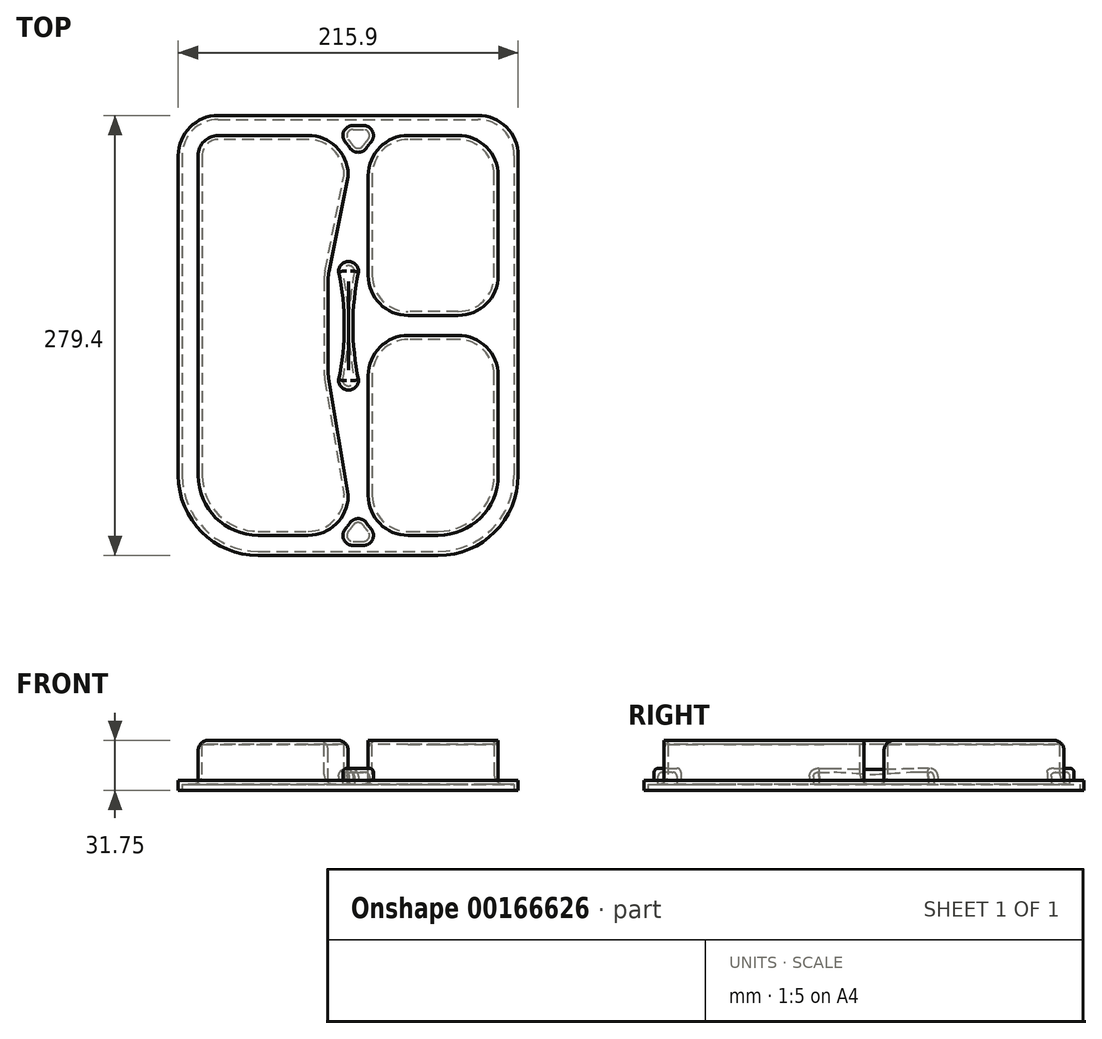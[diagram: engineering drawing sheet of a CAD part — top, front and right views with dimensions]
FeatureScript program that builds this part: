
annotation { "Feature Type Name" : "Feature", "Feature Type Description" : "" }
export const myFeature = defineFeature(function(context is Context, id is Id, definition is map)
    precondition{}
    {
        {
            var Q0;
            Q0=qCreatedBy(makeId("Top.planeOp"),FACE);
            var sketch = newSketch(context, id + "F0", { "sketchPlane" : qUnion([Q0])});
            skLineSegment(sketch, "E0.bottom", {"start": v(-121.24, 224.08) * mm, "end": v(43.86, 224.08) * mm});
            skLineSegment(sketch, "E0.top", {"start": v(-95.84, -55.32) * mm, "end": v(18.46, -55.32) * mm});
            skLineSegment(sketch, "E0.left", {"start": v(-146.64, 198.68) * mm, "end": v(-146.64, -4.52) * mm});
            skLineSegment(sketch, "E0.right", {"start": v(69.26, 198.68) * mm, "end": v(69.26, -4.52) * mm});
            skPoint(sketch, "E1.visualSharp", {"position": v(69.26, 224.08) * mm});
            skArc(sketch, "E1.filletArc", {"start": v(69.26, 198.68) * mm, "mid": v(61.83, 216.64) * mm, "end": v(43.86, 224.08) * mm});
            skPoint(sketch, "E2.visualSharp", {"position": v(-146.64, 224.08) * mm});
            skArc(sketch, "E2.filletArc", {"start": v(-121.24, 224.08) * mm, "mid": v(-139.2, 216.64) * mm, "end": v(-146.64, 198.68) * mm});
            skPoint(sketch, "E3.visualSharp", {"position": v(-146.64, -55.32) * mm});
            skArc(sketch, "E3.filletArc", {"start": v(-146.64, -4.52) * mm, "mid": v(-131.76, -40.44) * mm, "end": v(-95.84, -55.32) * mm});
            skPoint(sketch, "E4.visualSharp", {"position": v(69.26, -55.32) * mm});
            skArc(sketch, "E4.filletArc", {"start": v(18.46, -55.32) * mm, "mid": v(54.39, -40.44) * mm, "end": v(69.26, -4.52) * mm});
            skSolve(sketch);
        }
        {
            var Q0;
            Q0=makeQuery(id+"F0.imprint","IMPRINT",FACE,{"disambiguationData":[TD([[makeQuery(id+"F0.imprint","IMPRINT",EDGE,{"derivedFrom":sQuery(id+"F0.wireOp",EDGE,"E0.bottom")}),-1.0]])]});
            extrude(context, id + "F1", {"entities" : qUnion([Q0]), "depth" : 31.75 * mm});
        }
        {
            var Q0;
            Q0=makeQuery(id+"F1.opExtrude","CAP_FACE",FACE,{"disambiguationData":[OSD([sQuery(id+"F0.wireOp",EDGE,"E0.bottom"),sQuery(id+"F0.wireOp",EDGE,"E0.top"),sQuery(id+"F0.wireOp",EDGE,"E0.left"),sQuery(id+"F0.wireOp",EDGE,"E0.right"),sQuery(id+"F0.wireOp",EDGE,"E1.filletArc"),sQuery(id+"F0.wireOp",EDGE,"E2.filletArc"),sQuery(id+"F0.wireOp",EDGE,"E3.filletArc"),sQuery(id+"F0.wireOp",EDGE,"E4.filletArc")])],"isStart":false});
            var sketch = newSketch(context, id + "F2", { "sketchPlane" : qUnion([Q0])});
            skLineSegment(sketch, "E5.0.0", {"start": v(43.86, 224.08) * mm, "end": v(-121.24, 224.08) * mm});
            skArc(sketch, "E5.0.1", {"start": v(-121.24, 224.08) * mm, "mid": v(-139.2, 216.64) * mm, "end": v(-146.64, 198.68) * mm});
            skLineSegment(sketch, "E5.0.2", {"start": v(-146.64, 198.68) * mm, "end": v(-146.64, -4.52) * mm});
            skArc(sketch, "E5.0.3", {"start": v(-146.64, -4.52) * mm, "mid": v(-131.76, -40.44) * mm, "end": v(-95.84, -55.32) * mm});
            skLineSegment(sketch, "E5.0.4", {"start": v(-95.84, -55.32) * mm, "end": v(18.46, -55.32) * mm});
            skArc(sketch, "E5.0.5", {"start": v(18.46, -55.32) * mm, "mid": v(54.39, -40.44) * mm, "end": v(69.26, -4.52) * mm});
            skLineSegment(sketch, "E5.0.6", {"start": v(69.26, -4.52) * mm, "end": v(69.26, 198.68) * mm});
            skArc(sketch, "E5.0.7", {"start": v(69.26, 198.68) * mm, "mid": v(61.83, 216.64) * mm, "end": v(43.86, 224.08) * mm});
            skArc(sketch, "E6.0", {"start": v(18.46, -42.62) * mm, "mid": v(45.4, -31.46) * mm, "end": v(56.56, -4.52) * mm});
            skLineSegment(sketch, "E6.1", {"start": v(-95.84, -42.62) * mm, "end": v(-64.09, -42.62) * mm});
            skLineSegment(sketch, "E6.2", {"start": v(56.56, -4.52) * mm, "end": v(56.56, 58.98) * mm});
            skArc(sketch, "E6.3", {"start": v(-133.94, -4.52) * mm, "mid": v(-122.78, -31.46) * mm, "end": v(-95.84, -42.62) * mm});
            skLineSegment(sketch, "E6.5", {"start": v(31.16, 211.38) * mm, "end": v(-0.59, 211.38) * mm});
            skArc(sketch, "E6.6", {"start": v(-121.24, 211.38) * mm, "mid": v(-130.22, 207.66) * mm, "end": v(-133.94, 198.68) * mm});
            skLineSegment(sketch, "E6.7", {"start": v(-133.94, 198.68) * mm, "end": v(-133.94, -4.52) * mm});
            skLineSegment(sketch, "E7.0", {"start": v(-25.99, 185.98) * mm, "end": v(-25.99, 122.48) * mm});
            skLineSegment(sketch, "E8", {"start": v(31.16, 97.08) * mm, "end": v(-0.59, 97.08) * mm});
            skLineSegment(sketch, "E9.0", {"start": v(31.16, 84.38) * mm, "end": v(-0.59, 84.38) * mm});
            skPoint(sketch, "E10.orphan", {"position": v(-133.94, 97.08) * mm});
            skLineSegment(sketch, "E11.trimOffspring", {"start": v(-0.59, -42.62) * mm, "end": v(18.46, -42.62) * mm});
            skLineSegment(sketch, "E12.trimOffspring", {"start": v(-64.09, 211.38) * mm, "end": v(-121.24, 211.38) * mm});
            skLineSegment(sketch, "E13.trimOffspring", {"start": v(-25.99, 58.98) * mm, "end": v(-25.99, -17.22) * mm});
            skLineSegment(sketch, "E14.trimOffspring", {"start": v(56.56, 122.48) * mm, "end": v(56.56, 185.98) * mm});
            skPoint(sketch, "E15.visualSharp", {"position": v(-25.99, 211.38) * mm});
            skArc(sketch, "E15.filletArc", {"start": v(-0.59, 211.38) * mm, "mid": v(-18.55, 203.94) * mm, "end": v(-25.99, 185.98) * mm});
            skPoint(sketch, "E16.visualSharp", {"position": v(56.56, 97.08) * mm});
            skArc(sketch, "E16.filletArc", {"start": v(31.16, 97.08) * mm, "mid": v(49.13, 104.52) * mm, "end": v(56.56, 122.48) * mm});
            skPoint(sketch, "E17.visualSharp", {"position": v(-25.99, 97.08) * mm});
            skArc(sketch, "E17.filletArc", {"start": v(-25.99, 122.48) * mm, "mid": v(-18.55, 104.52) * mm, "end": v(-0.59, 97.08) * mm});
            skPoint(sketch, "E18.newPointA", {"position": v(56.56, 198.68) * mm});
            skPoint(sketch, "E18.newPointB", {"position": v(43.86, 211.38) * mm});
            skArc(sketch, "E18.filletArc", {"start": v(56.56, 185.98) * mm, "mid": v(49.13, 203.94) * mm, "end": v(31.16, 211.38) * mm});
            skPoint(sketch, "E19.visualSharp", {"position": v(56.56, 84.38) * mm});
            skArc(sketch, "E19.filletArc", {"start": v(56.56, 58.98) * mm, "mid": v(49.13, 76.94) * mm, "end": v(31.16, 84.38) * mm});
            skPoint(sketch, "E20.visualSharp", {"position": v(-25.99, 84.38) * mm});
            skArc(sketch, "E20.filletArc", {"start": v(-0.59, 84.38) * mm, "mid": v(-18.55, 76.94) * mm, "end": v(-25.99, 58.98) * mm});
            skPoint(sketch, "E21.visualSharp", {"position": v(-25.99, -42.62) * mm});
            skArc(sketch, "E21.filletArc", {"start": v(-25.99, -17.22) * mm, "mid": v(-18.55, -35.18) * mm, "end": v(-0.59, -42.62) * mm});
            skPoint(sketch, "E22.visualSharp", {"position": v(-38.69, -42.62) * mm});
            skArc(sketch, "E22.filletArc", {"start": v(-64.09, -42.62) * mm, "mid": v(-46.36, -35.41) * mm, "end": v(-38.7, -17.87) * mm});
            skPoint(sketch, "E23.visualSharp", {"position": v(-38.69, 211.38) * mm});
            skArc(sketch, "E23.filletArc", {"start": v(-38.7, 186.76) * mm, "mid": v(-46.4, 204.21) * mm, "end": v(-64.09, 211.38) * mm});
            skLineSegment(sketch, "E24", {"start": v(-25.99, 122.48) * mm, "end": v(-25.99, 58.98) * mm});
            skLineSegment(sketch, "E25.MirrorCS", {"start": v(-51.39, 119.96) * mm, "end": v(-51.39, 61.08) * mm});
            skLineSegment(sketch, "E26", {"start": v(-51.04, 56.9) * mm, "end": v(-38.78, -16.67) * mm});
            skLineSegment(sketch, "E27", {"start": v(-50.9, 124.94) * mm, "end": v(-38.82, 185.32) * mm});
            skPoint(sketch, "E28.visualSharp", {"position": v(-51.39, 122.48) * mm});
            skArc(sketch, "E28.filletArc", {"start": v(-50.9, 124.94) * mm, "mid": v(-51.26, 122.46) * mm, "end": v(-51.39, 119.96) * mm});
            skPoint(sketch, "E29.visualSharp", {"position": v(-51.39, 58.98) * mm});
            skArc(sketch, "E29.filletArc", {"start": v(-51.39, 61.08) * mm, "mid": v(-51.3, 58.98) * mm, "end": v(-51.04, 56.9) * mm});
            skPoint(sketch, "E30.visualSharp", {"position": v(-38.69, -17.22) * mm});
            skArc(sketch, "E30.filletArc", {"start": v(-38.7, -17.87) * mm, "mid": v(-38.7, -17.27) * mm, "end": v(-38.78, -16.67) * mm});
            skPoint(sketch, "E31.visualSharp", {"position": v(-38.69, 185.98) * mm});
            skArc(sketch, "E31.filletArc", {"start": v(-38.82, 185.32) * mm, "mid": v(-38.72, 186.03) * mm, "end": v(-38.7, 186.76) * mm});
            skSolve(sketch);
        }
        {
            var Q0;
            Q0=makeQuery(id+"F2.imprint","IMPRINT",FACE,{"disambiguationData":[TD([[makeQuery(id+"F2.imprint","IMPRINT",EDGE,{"derivedFrom":sQuery(id+"F2.wireOp",EDGE,"E5.0.0")}),-1.0]])]});
            extrude(context, id + "F3", {"entities" : qUnion([Q0]), "operationType" : NewBodyOperationType.REMOVE, "oppositeDirection" : true, "depth" : 25.4 * mm});
        }
        {
            var Q0;
            Q0=makeQuery(id+"F3.boolean.opBoolean","COPY",FACE,{"derivedFrom":makeQuery(id+"F3.opExtrude","CAP_FACE",FACE,{"disambiguationData":[OSD([sQuery(id+"F2.wireOp",EDGE,"E5.0.0"),sQuery(id+"F2.wireOp",EDGE,"E5.0.1"),sQuery(id+"F2.wireOp",EDGE,"E5.0.2"),sQuery(id+"F2.wireOp",EDGE,"E5.0.3"),sQuery(id+"F2.wireOp",EDGE,"E5.0.4"),sQuery(id+"F2.wireOp",EDGE,"E5.0.5"),sQuery(id+"F2.wireOp",EDGE,"E5.0.6"),sQuery(id+"F2.wireOp",EDGE,"E5.0.7"),sQuery(id+"F2.wireOp",EDGE,"E6.0"),sQuery(id+"F2.wireOp",EDGE,"E6.1"),sQuery(id+"F2.wireOp",EDGE,"E6.2"),sQuery(id+"F2.wireOp",EDGE,"E6.3"),sQuery(id+"F2.wireOp",EDGE,"E6.5"),sQuery(id+"F2.wireOp",EDGE,"E6.6"),sQuery(id+"F2.wireOp",EDGE,"E6.7"),sQuery(id+"F2.wireOp",EDGE,"E7.0"),sQuery(id+"F2.wireOp",EDGE,"E8"),sQuery(id+"F2.wireOp",EDGE,"E9.0"),sQuery(id+"F2.wireOp",EDGE,"E11.trimOffspring"),sQuery(id+"F2.wireOp",EDGE,"E12.trimOffspring"),sQuery(id+"F2.wireOp",EDGE,"E13.trimOffspring"),sQuery(id+"F2.wireOp",EDGE,"E14.trimOffspring"),sQuery(id+"F2.wireOp",EDGE,"E15.filletArc"),sQuery(id+"F2.wireOp",EDGE,"E16.filletArc"),sQuery(id+"F2.wireOp",EDGE,"E17.filletArc"),sQuery(id+"F2.wireOp",EDGE,"E18.filletArc"),sQuery(id+"F2.wireOp",EDGE,"E19.filletArc"),sQuery(id+"F2.wireOp",EDGE,"E20.filletArc"),sQuery(id+"F2.wireOp",EDGE,"E21.filletArc"),sQuery(id+"F2.wireOp",EDGE,"E22.filletArc"),sQuery(id+"F2.wireOp",EDGE,"E23.filletArc"),sQuery(id+"F2.wireOp",EDGE,"E25.MirrorCS"),sQuery(id+"F2.wireOp",EDGE,"E26"),sQuery(id+"F2.wireOp",EDGE,"E27"),sQuery(id+"F2.wireOp",EDGE,"E28.filletArc"),sQuery(id+"F2.wireOp",EDGE,"E29.filletArc"),sQuery(id+"F2.wireOp",EDGE,"E30.filletArc"),sQuery(id+"F2.wireOp",EDGE,"E31.filletArc")])],"isStart":false})});
            var sketch = newSketch(context, id + "F4", { "sketchPlane" : qUnion([Q0])});
            skPoint(sketch, "E32.orphan", {"position": v(-15.61, 124.94) * mm});
            skPoint(sketch, "E33.orphan", {"position": v(-25.99, 185.98) * mm});
            skArc(sketch, "E34", {"start": v(-32.08, 124.94) * mm, "mid": v(-38.44, 131.3) * mm, "end": v(-44.8, 124.94) * mm});
            skArc(sketch, "E35.MirrorC", {"start": v(-32.08, 56.1) * mm, "mid": v(-38.44, 49.74) * mm, "end": v(-44.8, 56.1) * mm});
            skArc(sketch, "E36", {"start": v(-44.8, 56.1) * mm, "mid": v(-41.2, 90.52) * mm, "end": v(-44.8, 124.94) * mm});
            skArc(sketch, "E37.MirrorCS", {"start": v(-32.08, 56.1) * mm, "mid": v(-35.68, 90.52) * mm, "end": v(-32.08, 124.94) * mm});
            skPoint(sketch, "E38.0", {"position": v(-46.4, 204.21) * mm});
            skLineSegment(sketch, "E39.0", {"start": v(-35.69, 217.73) * mm, "end": v(-28.98, 217.73) * mm});
            skArc(sketch, "E40.0", {"start": v(-37.63, 203.53) * mm, "mid": v(-38.96, 205.39) * mm, "end": v(-40.42, 207.14) * mm});
            skArc(sketch, "E41.0", {"start": v(-24.25, 207.14) * mm, "mid": v(-25.71, 205.39) * mm, "end": v(-27.04, 203.53) * mm});
            skPoint(sketch, "E42.orphan", {"position": v(-64.09, 211.38) * mm});
            skPoint(sketch, "E43.0.start.orphan", {"position": v(-38.7, 186.76) * mm});
            skPoint(sketch, "E44.0.start.orphan", {"position": v(-0.59, 211.38) * mm});
            skPoint(sketch, "E45.visualSharp", {"position": v(-64.09, 217.73) * mm});
            skArc(sketch, "E45.filletArc", {"start": v(-35.69, 217.73) * mm, "mid": v(-41.48, 213.97) * mm, "end": v(-40.42, 207.14) * mm});
            skPoint(sketch, "E46.visualSharp", {"position": v(-0.59, 217.73) * mm});
            skArc(sketch, "E46.filletArc", {"start": v(-24.25, 207.14) * mm, "mid": v(-23.19, 213.97) * mm, "end": v(-28.98, 217.73) * mm});
            skArc(sketch, "E47.filletArc", {"start": v(-37.63, 203.53) * mm, "mid": v(-32.34, 200.69) * mm, "end": v(-27.04, 203.53) * mm});
            skLineSegment(sketch, "E48", {"start": v(15.29, 97.08) * mm, "end": v(15.29, 84.38) * mm, "construction": true});
            skLineSegment(sketch, "E49", {"start": v(15.29, 90.73) * mm, "end": v(111.89, 90.73) * mm, "construction": true});
            skPoint(sketch, "E50.MirrorP", {"position": v(-64.09, -36.27) * mm});
            skPoint(sketch, "E51.MirrorP", {"position": v(-64.09, -29.92) * mm});
            skArc(sketch, "E52.0", {"start": v(-40.42, -38.4) * mm, "mid": v(-38.96, -36.63) * mm, "end": v(-37.63, -34.77) * mm});
            skArc(sketch, "E53.0", {"start": v(-27.04, -34.77) * mm, "mid": v(-25.71, -36.63) * mm, "end": v(-24.25, -38.4) * mm});
            skLineSegment(sketch, "E54.0", {"start": v(-35.69, -48.97) * mm, "end": v(-28.98, -48.97) * mm});
            skArc(sketch, "E55.filletArc", {"start": v(-27.04, -34.77) * mm, "mid": v(-32.34, -31.93) * mm, "end": v(-37.63, -34.77) * mm});
            skArc(sketch, "E56.filletArc", {"start": v(-40.42, -38.4) * mm, "mid": v(-41.48, -45.22) * mm, "end": v(-35.69, -48.97) * mm});
            skArc(sketch, "E57.filletArc", {"start": v(-28.98, -48.97) * mm, "mid": v(-23.19, -45.22) * mm, "end": v(-24.25, -38.4) * mm});
            skSolve(sketch);
        }
        {
            var Q0;
            Q0=makeQuery(id+"F4.imprint","IMPRINT",FACE,{"disambiguationData":[TD([[makeQuery(id+"F4.imprint","IMPRINT",EDGE,{"derivedFrom":sQuery(id+"F4.wireOp",EDGE,"E34")}),1.0]])]});
            var Q1;
            Q1=makeQuery(id+"F4.imprint","IMPRINT",FACE,{"disambiguationData":[TD([[makeQuery(id+"F4.imprint","IMPRINT",EDGE,{"derivedFrom":sQuery(id+"F4.wireOp",EDGE,"E52.0")}),-1.0]])]});
            var Q2;
            Q2=makeQuery(id+"F4.imprint","IMPRINT",FACE,{"disambiguationData":[TD([[makeQuery(id+"F4.imprint","IMPRINT",EDGE,{"derivedFrom":sQuery(id+"F4.wireOp",EDGE,"E39.0")}),-1.0]])]});
            extrude(context, id + "F5", {"entities" : qUnion([Q0, Q1, Q2]), "operationType" : NewBodyOperationType.ADD, "depth" : 7.62 * mm});
        }
        {
            var Q0;
            Q0=makeQuery(id+"F1.opExtrude","CAP_FACE",FACE,{"disambiguationData":[OSD([sQuery(id+"F0.wireOp",EDGE,"E0.bottom"),sQuery(id+"F0.wireOp",EDGE,"E0.top"),sQuery(id+"F0.wireOp",EDGE,"E0.left"),sQuery(id+"F0.wireOp",EDGE,"E0.right"),sQuery(id+"F0.wireOp",EDGE,"E1.filletArc"),sQuery(id+"F0.wireOp",EDGE,"E2.filletArc"),sQuery(id+"F0.wireOp",EDGE,"E3.filletArc"),sQuery(id+"F0.wireOp",EDGE,"E4.filletArc")])],"isStart":true});
            shell(context, id + "F6", {"entities" : qUnion([Q0]), "thickness" : 2.54 * mm});
        }
        {
            var Q0;
            {var subQ0=sQuery(id+"F2.wireOp",EDGE,"E6.7");Q0=makeQuery(id+"F6.opShell","OFFSET_EDGE",EDGE,{"disambiguationData":[OSD([subQ0]),TDD([makeQuery(id+"F3.boolean.opBoolean","COPY",EDGE,{"derivedFrom":makeQuery(id+"F3.opExtrude","CAP_EDGE",EDGE,{"disambiguationData":[OSD([subQ0])],"isStart":false})})])]});}
            var Q1;
            {var subQ0=sQuery(id+"F2.wireOp",EDGE,"E7.0");Q1=makeQuery(id+"F6.opShell","OFFSET_EDGE",EDGE,{"disambiguationData":[OSD([subQ0]),TDD([makeQuery(id+"F3.boolean.opBoolean","COPY",EDGE,{"derivedFrom":makeQuery(id+"F3.opExtrude","CAP_EDGE",EDGE,{"disambiguationData":[OSD([subQ0])],"isStart":false})})])]});}
            var Q2;
            {var subQ0=sQuery(id+"F2.wireOp",EDGE,"E13.trimOffspring");Q2=makeQuery(id+"F6.opShell","OFFSET_EDGE",EDGE,{"disambiguationData":[OSD([subQ0]),TDD([makeQuery(id+"F3.boolean.opBoolean","COPY",EDGE,{"derivedFrom":makeQuery(id+"F3.opExtrude","CAP_EDGE",EDGE,{"disambiguationData":[OSD([subQ0])],"isStart":false})})])]});}
            fillet(context, id + "F7", {"entities" : qUnion([Q0, Q1, Q2]), "radius" : 6.35 * mm, "tangentPropagation" : true, "allowEdgeOverflow" : false});
        }
        {
            var Q0;
            Q0=makeQuery(id+"F3.boolean.opBoolean","COPY",EDGE,{"derivedFrom":makeQuery(id+"F3.opExtrude","CAP_EDGE",EDGE,{"disambiguationData":[OSD([sQuery(id+"F2.wireOp",EDGE,"E12.trimOffspring")])],"isStart":true})});
            var Q1;
            Q1=makeQuery(id+"F3.boolean.opBoolean","COPY",EDGE,{"derivedFrom":makeQuery(id+"F3.opExtrude","CAP_EDGE",EDGE,{"disambiguationData":[OSD([sQuery(id+"F2.wireOp",EDGE,"E14.trimOffspring")])],"isStart":true})});
            var Q2;
            Q2=makeQuery(id+"F3.boolean.opBoolean","COPY",EDGE,{"derivedFrom":makeQuery(id+"F3.opExtrude","CAP_EDGE",EDGE,{"disambiguationData":[OSD([sQuery(id+"F2.wireOp",EDGE,"E6.2")])],"isStart":true})});
            fillet(context, id + "F8", {"entities" : qUnion([Q0, Q1, Q2]), "radius" : 6.35 * mm, "tangentPropagation" : true, "allowEdgeOverflow" : false});
        }
        {
            var Q0;
            {var subQ0=sQuery(id+"F4.wireOp",EDGE,"E34");Q0=makeQuery(id+"F6.opShell","OFFSET_EDGE",EDGE,{"disambiguationData":[OSD([subQ0]),TDD([makeQuery(id+"F5.opExtrude","CAP_EDGE",EDGE,{"disambiguationData":[OSD([subQ0])],"isStart":true})])]});}
            var Q1;
            {var subQ0=sQuery(id+"F4.wireOp",EDGE,"E35.MirrorC");Q1=makeQuery(id+"F6.opShell","OFFSET_EDGE",EDGE,{"disambiguationData":[OSD([subQ0]),TDD([makeQuery(id+"F5.opExtrude","CAP_EDGE",EDGE,{"disambiguationData":[OSD([subQ0])],"isStart":true})])]});}
            var Q2;
            {var subQ0=sQuery(id+"F4.wireOp",EDGE,"E36");Q2=makeQuery(id+"F6.opShell","OFFSET_EDGE",EDGE,{"disambiguationData":[OSD([subQ0]),TDD([makeQuery(id+"F5.opExtrude","CAP_EDGE",EDGE,{"disambiguationData":[OSD([subQ0])],"isStart":true})])]});}
            var Q3;
            {var subQ0=sQuery(id+"F4.wireOp",EDGE,"E37.MirrorCS");Q3=makeQuery(id+"F6.opShell","OFFSET_EDGE",EDGE,{"disambiguationData":[OSD([subQ0]),TDD([makeQuery(id+"F5.opExtrude","CAP_EDGE",EDGE,{"disambiguationData":[OSD([subQ0])],"isStart":true})])]});}
            var Q4;
            {var subQ0=sQuery(id+"F4.wireOp",EDGE,"E39.0");Q4=makeQuery(id+"F6.opShell","OFFSET_EDGE",EDGE,{"disambiguationData":[OSD([subQ0]),TDD([makeQuery(id+"F5.opExtrude","CAP_EDGE",EDGE,{"disambiguationData":[OSD([subQ0])],"isStart":true})])]});}
            var Q5;
            {var subQ0=sQuery(id+"F4.wireOp",EDGE,"E55.filletArc");Q5=makeQuery(id+"F6.opShell","OFFSET_EDGE",EDGE,{"disambiguationData":[OSD([subQ0]),TDD([makeQuery(id+"F5.opExtrude","CAP_EDGE",EDGE,{"disambiguationData":[OSD([subQ0])],"isStart":true})])]});}
            fillet(context, id + "F9", {"entities" : qUnion([Q0, Q1, Q2, Q3, Q4, Q5]), "radius" : 2.54 * mm, "tangentPropagation" : true, "allowEdgeOverflow" : false});
        }
        {
            var Q0;
            Q0=makeQuery(id+"F5.opExtrude","CAP_EDGE",EDGE,{"disambiguationData":[OSD([sQuery(id+"F4.wireOp",EDGE,"E54.0")])],"isStart":false});
            var Q1;
            Q1=makeQuery(id+"F5.opExtrude","CAP_EDGE",EDGE,{"disambiguationData":[OSD([sQuery(id+"F4.wireOp",EDGE,"E45.filletArc")])],"isStart":false});
            fillet(context, id + "F10", {"entities" : qUnion([Q0, Q1]), "radius" : 2.54 * mm, "tangentPropagation" : true, "allowEdgeOverflow" : false});
        }
        {
            var Q0;
            Q0=makeQuery(id+"F5.opExtrude","CAP_EDGE",EDGE,{"disambiguationData":[OSD([sQuery(id+"F4.wireOp",EDGE,"E37.MirrorCS")])],"isStart":false});
            var Q1;
            Q1=makeQuery(id+"F5.opExtrude","CAP_EDGE",EDGE,{"disambiguationData":[OSD([sQuery(id+"F4.wireOp",EDGE,"E36")])],"isStart":false});
            var Q2;
            Q2=makeQuery(id+"F5.opExtrude","CAP_EDGE",EDGE,{"disambiguationData":[OSD([sQuery(id+"F4.wireOp",EDGE,"E34")])],"isStart":false});
            var Q3;
            Q3=makeQuery(id+"F5.opExtrude","CAP_EDGE",EDGE,{"disambiguationData":[OSD([sQuery(id+"F4.wireOp",EDGE,"E35.MirrorC")])],"isStart":false});
            fillet(context, id + "F11", {"entities" : qUnion([Q0, Q1, Q2, Q3]), "radius" : 5.08 * mm, "tangentPropagation" : true, "allowEdgeOverflow" : false});
        }
    });
